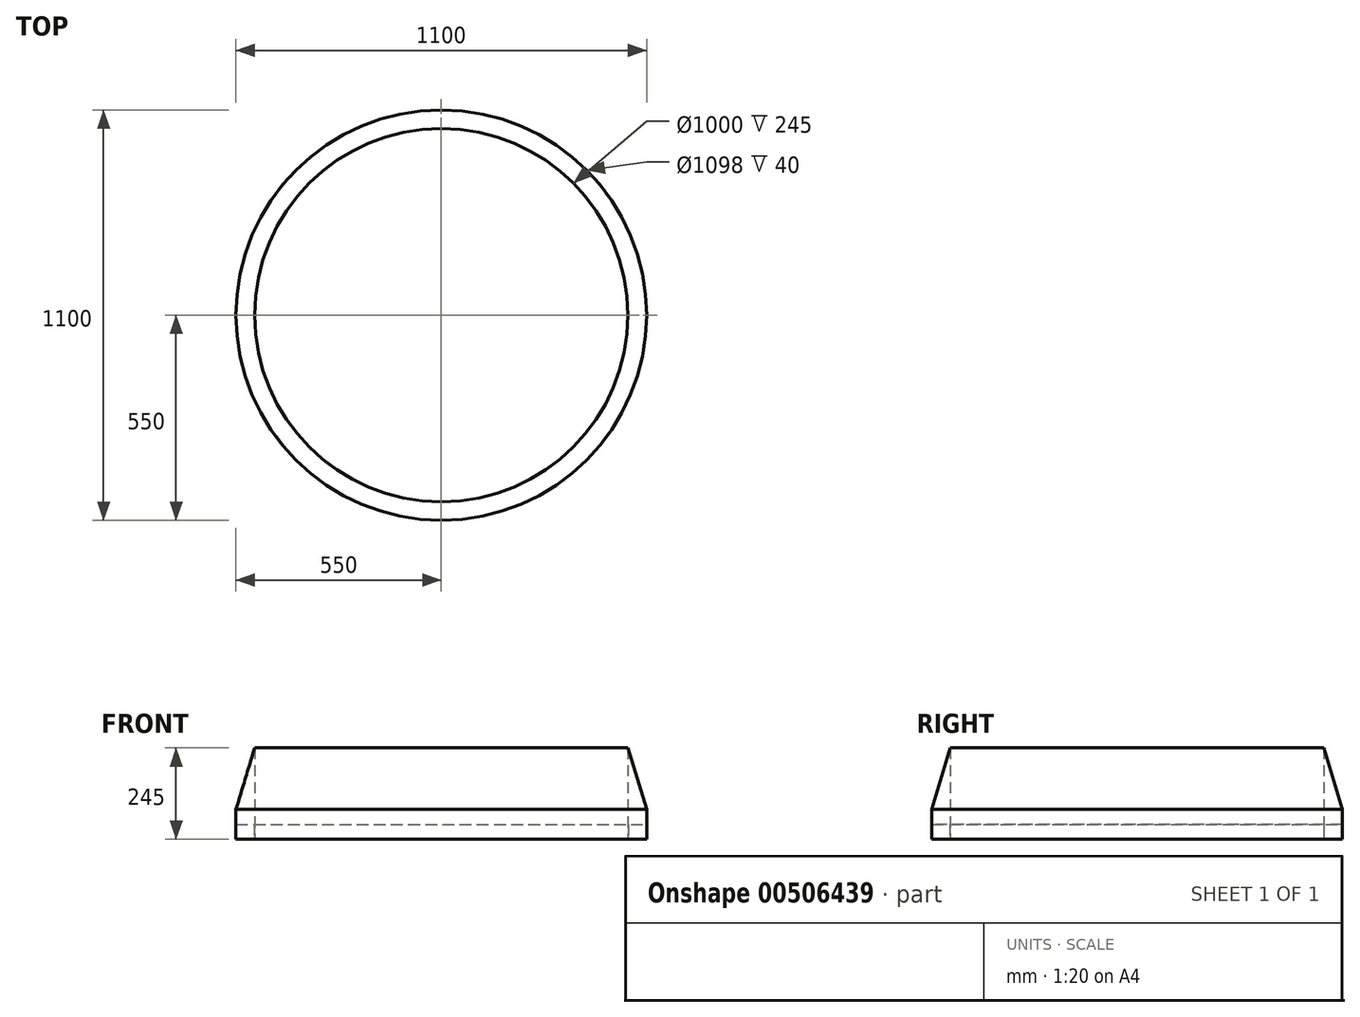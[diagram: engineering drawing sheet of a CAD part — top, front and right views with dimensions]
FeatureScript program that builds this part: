
annotation { "Feature Type Name" : "Feature", "Feature Type Description" : "" }
export const myFeature = defineFeature(function(context is Context, id is Id, definition is map)
    precondition{}
    {
        {
            var Q0;
            Q0=qCreatedBy(makeId("Front.planeOp"),FACE);
            var sketch = newSketch(context, id + "F0", { "sketchPlane" : qUnion([Q0])});
            skLineSegment(sketch, "E0", {"start": v(0, -139.25) * mm, "end": v(0, 240.83) * mm, "construction": true});
            skLineSegment(sketch, "E1", {"start": v(-500, -67.22) * mm, "end": v(-500, 177.78) * mm});
            skLineSegment(sketch, "E2", {"start": v(-500, 177.78) * mm, "end": v(-550, 12.78) * mm});
            skLineSegment(sketch, "E3", {"start": v(-550, 12.78) * mm, "end": v(-550, -67.22) * mm});
            skLineSegment(sketch, "E4", {"start": v(-550, -67.22) * mm, "end": v(-549, -67.22) * mm});
            skLineSegment(sketch, "E5", {"start": v(-549, -67.22) * mm, "end": v(-549, -27.22) * mm});
            skLineSegment(sketch, "E6", {"start": v(-549, -27.22) * mm, "end": v(-501, -27.22) * mm});
            skLineSegment(sketch, "E7", {"start": v(-501, -27.22) * mm, "end": v(-501, -67.22) * mm});
            skLineSegment(sketch, "E8", {"start": v(-501, -67.22) * mm, "end": v(-500, -67.22) * mm});
            skSolve(sketch);
        }
        {
            var Q0;
            Q0 = qSketchRegion(id + "F0", true);
            var Q1;
            Q1=sQuery(id+"F0.wireOp",EDGE,"E0");
            revolve(context, id + "F1", {"entities" : qUnion([Q0]), "axis" : qUnion([Q1]), "revolveType" : RevolveType.FULL});
        }
    });
